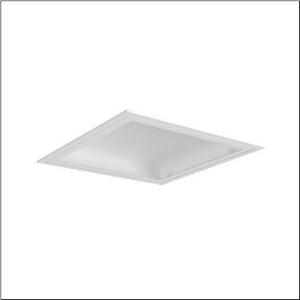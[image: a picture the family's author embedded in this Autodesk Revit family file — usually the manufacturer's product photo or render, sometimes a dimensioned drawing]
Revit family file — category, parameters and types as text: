
# Revit family: mira_r__21_51fr427a432a_cde4
name_source: partatom
category: Lighting Fixtures
units: mm (PartAtom-declared; Revit-internal decimal feet)

## family parameters
Cut with Voids When Loaded = No
Host = Face
Light Source = No
Part Type = Normal
Room Calculation Point = No
Round Connector Dimension = Use Diameter
Shared = No

## types (1)
- Mira® 21 (1 x LED, 3220 lm, 23 W, 4000K)
    Apparent Load = 23 VA
    CIE Flux Codes = 50 81 97 100 100
    Color Rendering = 80
    Color Temperature = 4000K
    Default Elevation = 1800 mm
    Description = Mira® 21, clean room luminaire, primary light control with reflector, primary optical cover: cover, of PC, light emission: direct distribution, primary light characteristic: symmetric, installation type: recessed, LED, rated luminous flux: 3.220lm, luminous efficacy: 140lm/W, light colour: 840, colour temperature: 4000K, control gear: ON/OFF, with terminal, 3-pole, max. 2.5mm², mains connection: 230V, AC, 50/60Hz, rated input power: 23W, luminaire housing, of sheet steel, coated, pure white (RAL 9010), with concealed spring brackets, module: M625, length: 623mm, width: 623mm, height: 115mm, protection rating (complete): IP54, insulation class (complete): insulation class I (protective earthing), certification: CE, UKCA, permissible operating ambient temperature: -5..+40°C, standard: EN 50419, packaging unit: 1 piece
    Height = 0 mm  [stored 0 ft]
    Lamp = 1 x LED
    Lamp Light Flux = 3220 lm
    Lamp Power = 23 W
    Lamp count = 1
    Length = 625 mm
    Luminous efficacy = 140 lm/W
    Manufacturer = Siteco
    ModVariant = No
    Model = 51FR427A432A
    Mounting Place = Ceiling
    Mounting Type = Recessed
    Number of Poles = 1
    OnlyDefault = Yes
    Power Factor = 1
    Product Name = Mira® 21
    Product group = clean room luminaire | ceiling recessed
    ProductGroupID = 402
    Protection Class = Protection class I
    Protection Degree = IP 54
    RLX_Detail_Level = 1
    RLX_Emergency_Light_Flux = 0 lm
    RLX_Emergency_Type = 0
    RLX_Emergency_Type_DB = No
    RlxData = <blob elided: 13401 chars, md5=60f6ba43>
    Socket = socket
    Standby Power = 0 W
    System Light Flux = 3220 lm
    System Power = 23 W
    Type Comments = Product without accessories
    Type Image = l_1007109.jpg
    URL = http://relux.com
    VarID = ---
    Voltage = 0 V
    Weight = 0.00 kg
    Width = 625 mm

note: [stored X ft] marks values corroborated as IEEE doubles in the binary element streams (Revit-internal decimal feet)

## geometry (parser evidence)
native form markers: Sweep x8
no freeform markers — native parametric forms only
